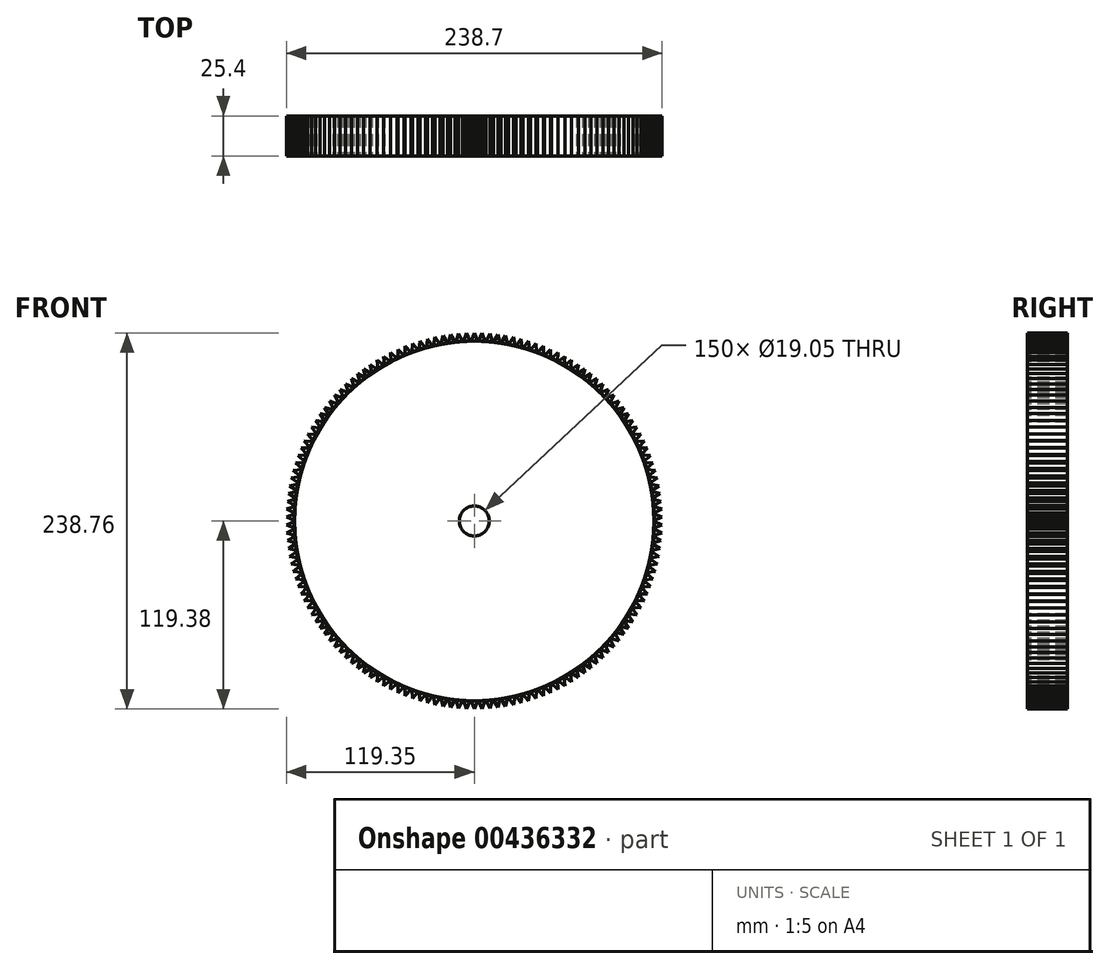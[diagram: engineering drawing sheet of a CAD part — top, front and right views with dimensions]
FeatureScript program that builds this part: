
annotation { "Feature Type Name" : "Feature", "Feature Type Description" : "" }
export const myFeature = defineFeature(function(context is Context, id is Id, definition is map)
    precondition{}
    {
        {
            var Q0;
            Q0=qCreatedBy(makeId("Front.planeOp"),FACE);
            var sketch = newSketch(context, id + "F0", { "sketchPlane" : qUnion([Q0])});
            skCircle(sketch, "E0", {"center": v(0, 0) * mm, "radius": 114.3 * mm});
            skCircle(sketch, "E1", {"center": v(0, 0) * mm, "radius": 9.53 * mm});
            skSolve(sketch);
        }
        {
            var Q0;
            Q0 = qSketchRegion(id + "F0", true);
            extrude(context, id + "F1", {"entities" : qUnion([Q0]), "endBound" : BoundingType.SYMMETRIC, "depth" : 25.4 * mm});
        }
        {
            var Q0;
            Q0=qCreatedBy(makeId("Right.planeOp"),FACE);
            var sketch = newSketch(context, id + "F2", { "sketchPlane" : qUnion([Q0])});
            skLineSegment(sketch, "E2", {"start": v(7.81, 0) * mm, "end": v(-18.62, 0) * mm});
            skSolve(sketch);
        }
        {
            var Q0;
            Q0=makeQuery(id+"F1.opExtrude","CAP_FACE",FACE,{"disambiguationData":[OSD([sQuery(id+"F0.wireOp",EDGE,"E0"),sQuery(id+"F0.wireOp",EDGE,"E1")])],"isStart":false});
            var sketch = newSketch(context, id + "F3", { "sketchPlane" : qUnion([Q0])});
            skLineSegment(sketch, "E3", {"start": v(0, 114.3) * mm, "end": v(0, 119.38) * mm});
            skLineSegment(sketch, "E4", {"start": v(0, 119.38) * mm, "end": v(-2.11, 114.28) * mm});
            skLineSegment(sketch, "E5", {"start": v(0, 119.38) * mm, "end": v(2.11, 114.28) * mm});
            skLineSegment(sketch, "E6", {"start": v(-2.11, 114.28) * mm, "end": v(2.11, 114.28) * mm});
            skSolve(sketch);
        }
        {
            var Q0;
            Q0 = qSketchRegion(id + "F3", true);
            extrude(context, id + "F4", {"entities" : qUnion([Q0]), "operationType" : NewBodyOperationType.ADD, "oppositeDirection" : true, "depth" : 25.4 * mm});
        }
        {
            var Q0;
            Q0=makeQuery(id+"F1.opExtrude","SWEPT_BODY",BODY,{"disambiguationData":[OSD([sQuery(id+"F0.wireOp",EDGE,"E0"),sQuery(id+"F0.wireOp",EDGE,"E1")])]});
            var Q1;
            Q1=sQuery(id+"F2.wireOp",EDGE,"E2");
            circularPattern(context, id + "F5", {"entities" : qUnion([Q0]), "axis" : qUnion([Q1]), "angle" : 360 * degree, "instanceCount" : 150, "equalSpace" : true});
        }
    });
